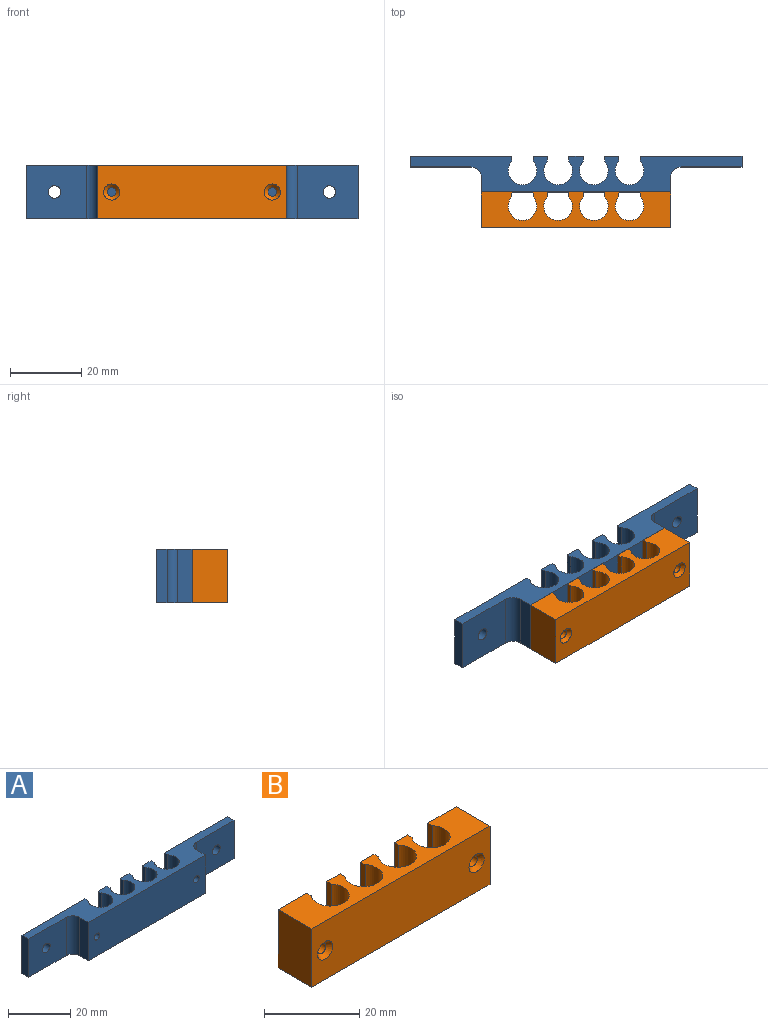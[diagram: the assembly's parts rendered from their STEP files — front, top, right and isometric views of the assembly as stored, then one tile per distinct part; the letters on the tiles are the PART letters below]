
ASSEMBLY  parts=2 mates=1
PART A: 34 faces, bbox 93x10x15 mm
  f0: plane 28.5x15mm, normal (0,1,0), area 417.9mm2, adj f1,f20,f21,f29,f32
  f1: plane 15x1.35mm, normal (-1,0,0), area 20.3mm2, adj f0,f2,f20,f21
  f2: cylinder r=4mm len=15mm, axis (0,0,-1), area 275.2mm2, adj f1,f3,f20,f21
  f3: plane 15x1.35mm, normal (1,0,0), area 20.3mm2, adj f2,f4,f20,f21
  f4: plane 15x4mm, normal (0,1,0), area 60mm2, adj f3,f5,f20,f21
  f5: plane 15x1.35mm, normal (-1,0,0), area 20.3mm2, adj f4,f6,f20,f21
  f6: cylinder r=4mm len=15mm, axis (0,0,-1), area 275.2mm2, adj f5,f7,f20,f21
  f7: plane 15x1.35mm, normal (1,0,0), area 20.3mm2, adj f6,f8,f20,f21
  f8: plane 15x4mm, normal (0,1,0), area 60mm2, adj f7,f9,f20,f21
  f9: plane 15x1.35mm, normal (-1,0,0), area 20.3mm2, adj f8,f10,f20,f21
  f10: cylinder r=4mm len=15mm, axis (0,0,-1), area 275.2mm2, adj f9,f11,f20,f21
  f11: plane 15x1.35mm, normal (1,0,0), area 20.3mm2, adj f10,f12,f20,f21
  f12: plane 15x4mm, normal (0,1,0), area 60mm2, adj f11,f13,f20,f21
  f13: plane 15x1.35mm, normal (-1,0,0), area 20.3mm2, adj f12,f14,f20,f21
  f14: cylinder r=4mm len=15mm, axis (0,0,-1), area 275.2mm2, adj f13,f15,f20,f21
  f15: plane 15x1.35mm, normal (1,0,0), area 20.3mm2, adj f14,f16,f20,f21
  f16: plane 28.5x15mm, normal (0,1,0), area 417.9mm2, adj f15,f20,f21,f26,f33
  f17: plane 15x4mm, normal (-1,0,0), area 60mm2, adj f18,f20,f21,f31
  f18: plane 53x15mm, normal (0,-1,0), area 785.2mm2, adj f17,f19,f20,f21,f22,f24
  f19: plane 15x4mm, normal (1,0,0), area 60mm2, adj f18,f20,f21,f30
  f20: plane 93x10mm, normal (0,0,1), area 442.8mm2, adj f0,f1,f2,f3,f4,f5,f6,f7
  f21: plane 93x10mm, normal (0,0,-1), area 442.8mm2, adj f0,f1,f2,f3,f4,f5,f6,f7
  f22: cylinder r=1.25mm len=8mm, axis (0,-1,0), area 62.8mm2, adj f18,f23
  f23: plane 2.5x2.5mm, normal (0,-1,0), area 4.9mm2, adj f22
  f24: cylinder r=1.25mm len=8mm, axis (0,-1,0), area 62.8mm2, adj f18,f25
  f25: plane 2.5x2.5mm, normal (0,-1,0), area 4.9mm2, adj f24
  f26: plane 15x3mm, normal (-1,0,0), area 45mm2, adj f16,f20,f21,f27
  f27: plane 17x15mm, normal (0,-1,0), area 245.4mm2, adj f20,f21,f26,f31,f33
  f28: plane 17x15mm, normal (0,-1,0), area 245.4mm2, adj f20,f21,f29,f30,f32
  f29: plane 15x3mm, normal (1,0,0), area 45mm2, adj f0,f20,f21,f28
  f30: cylinder r=3mm len=15mm, axis (0,0,1), area 70.7mm2, adj f19,f20,f21,f28
  f31: cylinder r=3mm len=15mm, axis (0,0,1), area 70.7mm2, adj f17,f20,f21,f27
  f32: cylinder r=1.75mm len=3.5mm, axis (0,-1,0), area 33mm2, adj f0,f28
  f33: cylinder r=1.75mm len=3.5mm, axis (0,-1,0), area 33mm2, adj f16,f27
PART B: 26 faces, bbox 53x10x15 mm
  f0: plane 15x10mm, normal (1,0,0), area 150mm2, adj f1,f19,f20,f21
  f1: plane 15x8.5mm, normal (0,1,0), area 122.6mm2, adj f0,f3,f20,f21,f22
  f2: plane 15x8.5mm, normal (0,1,0), area 122.6mm2, adj f17,f18,f20,f21,f23
  f3: plane 15x1.35mm, normal (-1,0,0), area 20.3mm2, adj f1,f4,f20,f21
  f4: cylinder r=4mm len=15mm, axis (0,0,-1), area 275.2mm2, adj f3,f5,f20,f21
  f5: plane 15x1.35mm, normal (1,0,0), area 20.3mm2, adj f4,f6,f20,f21
  f6: plane 15x4mm, normal (0,1,0), area 60mm2, adj f5,f7,f20,f21
  f7: plane 15x1.35mm, normal (-1,0,0), area 20.3mm2, adj f6,f8,f20,f21
  f8: cylinder r=4mm len=15mm, axis (0,0,-1), area 275.2mm2, adj f7,f9,f20,f21
  f9: plane 15x1.35mm, normal (1,0,0), area 20.3mm2, adj f8,f10,f20,f21
  f10: plane 15x4mm, normal (0,1,0), area 60mm2, adj f9,f11,f20,f21
  f11: plane 15x1.35mm, normal (-1,0,0), area 20.3mm2, adj f10,f12,f20,f21
  f12: cylinder r=4mm len=15mm, axis (0,0,-1), area 275.2mm2, adj f11,f13,f20,f21
  f13: plane 15x1.35mm, normal (1,0,0), area 20.3mm2, adj f12,f14,f20,f21
  f14: plane 15x4mm, normal (0,1,0), area 60mm2, adj f13,f15,f20,f21
  f15: plane 15x1.35mm, normal (-1,0,0), area 20.3mm2, adj f14,f16,f20,f21
  f16: cylinder r=4mm len=15mm, axis (0,0,-1), area 275.2mm2, adj f15,f17,f20,f21
  f17: plane 15x1.35mm, normal (1,0,0), area 20.3mm2, adj f2,f16,f20,f21
  f18: plane 15x10mm, normal (-1,0,0), area 150mm2, adj f2,f19,f20,f21
  f19: plane 53x15mm, normal (0,-1,0), area 763.2mm2, adj f0,f18,f20,f21,f24,f25
  f20: plane 53x10mm, normal (0,0,1), area 319mm2, adj f0,f1,f2,f3,f4,f5,f6,f7
  f21: plane 53x10mm, normal (0,0,-1), area 319mm2, adj f0,f1,f2,f3,f4,f5,f6,f7
  f22: cylinder r=1.25mm len=9mm, axis (0,-1,0), area 70.7mm2, adj f1,f24
  f23: cylinder r=1.25mm len=9mm, axis (0,-1,0), area 70.7mm2, adj f2,f25
  f24: cone r=1.25mm half-angle=45deg, axis (0,-1,0), area 15.6mm2, adj f19,f22
  f25: cone r=1.25mm half-angle=45deg, axis (0,-1,0), area 15.6mm2, adj f19,f23
PLACE A t=(0,5,-7.5)mm
PLACE B t=(0,-5,-7.5)mm
MATE fastened B.f22 <-> A.f22  axis (0,1,0) through (22.5,0,0)mm
